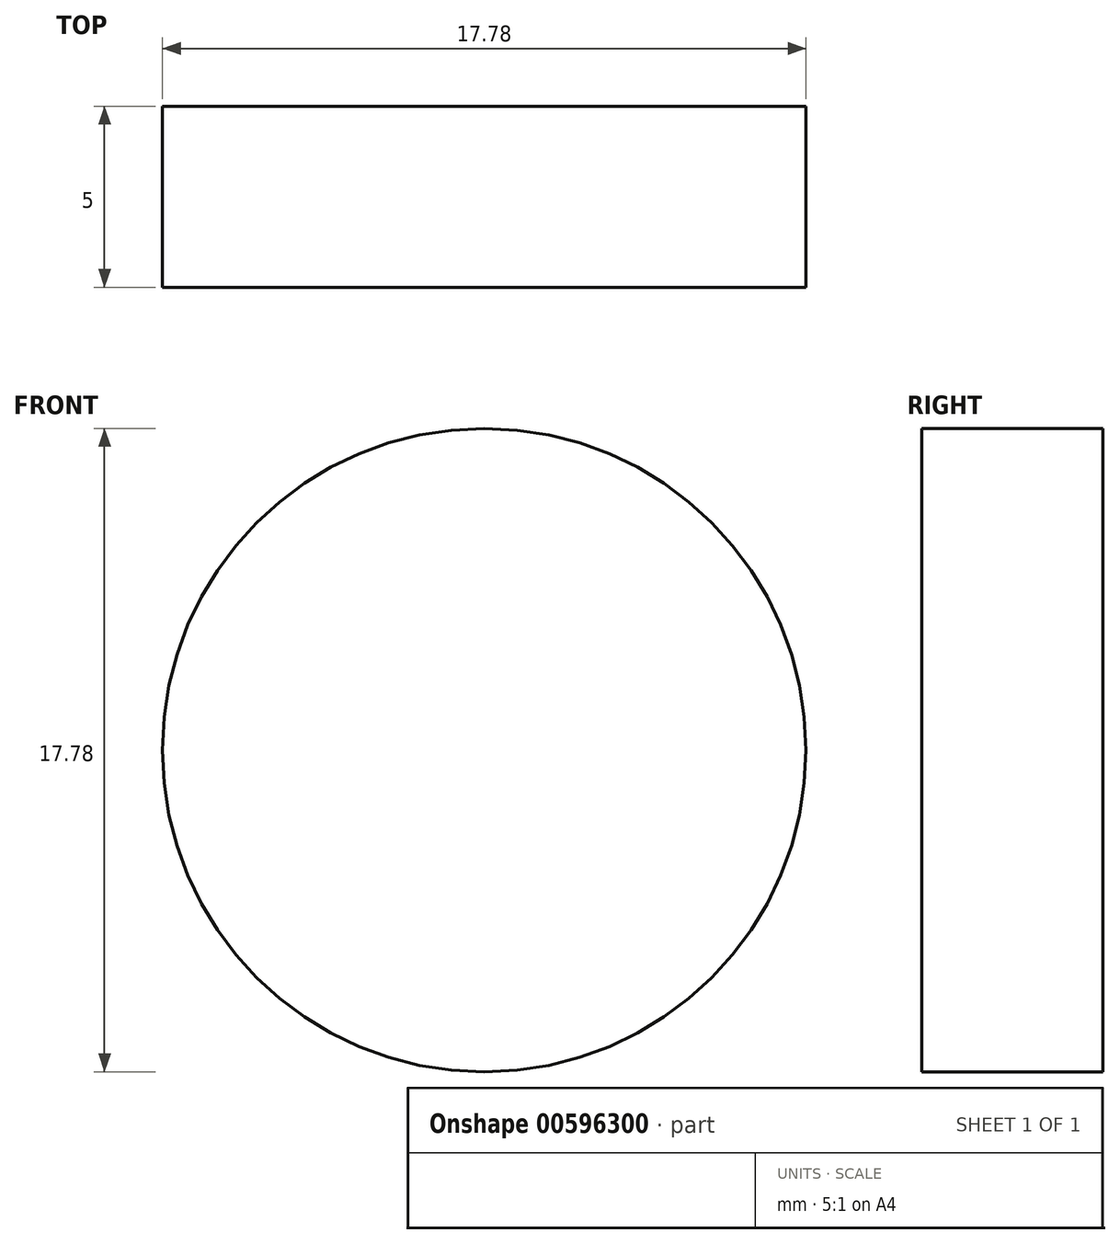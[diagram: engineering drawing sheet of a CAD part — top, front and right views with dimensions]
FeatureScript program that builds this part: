
annotation { "Feature Type Name" : "Feature", "Feature Type Description" : "" }
export const myFeature = defineFeature(function(context is Context, id is Id, definition is map)
    precondition{}
    {
        {
            var Q0;
            Q0=qCreatedBy(makeId("Front.planeOp"),FACE);
            var sketch = newSketch(context, id + "F0", { "sketchPlane" : qUnion([Q0])});
            skCircle(sketch, "E0", {"center": v(-36.51, 16.83) * mm, "radius": 8.89 * mm});
            skSolve(sketch);
        }
        {
            var Q0;
            Q0 = qSketchRegion(id + "F0", true);
            extrude(context, id + "F1", {"entities" : qUnion([Q0]), "depth" : 5 * mm, "offsetDistance" : 25 * mm});
        }
    });
